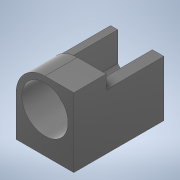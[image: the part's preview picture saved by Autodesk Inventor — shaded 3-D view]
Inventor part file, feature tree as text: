
AUTODESK INVENTOR PART (.ipt)
format: ipt  version: 2020 (Build 240168000, 168)  size: 143,360 bytes
history: native  units: in
note: dims shown in document units (in); Inventor stores cm internally (conversion verified against a paired STEP export)
features: extrude x2, sketch x1, projected_geometry x1
ambient origin geometry x8: Origin, YZ Plane, XZ Plane, XY Plane, X Axis, Y Axis, Z Axis, Center Point
bodies: Body1 (feature_tree)
feature tree (4):
  extrude  "Extrusion3"  Depth=0.0787in
  extrude  "Extrusion4"  Depth=0.4724in
  sketch  "Sketch5"  dims[d12=0.6299in d13=0.0787in d14=0.5512in d17=0.7874in d18=0.4429in d19=0.0in d22=0.7874in d23=0.0in d24=0.6102in d25=0.4724in]
  projected_geometry  "Projected Loop1"
